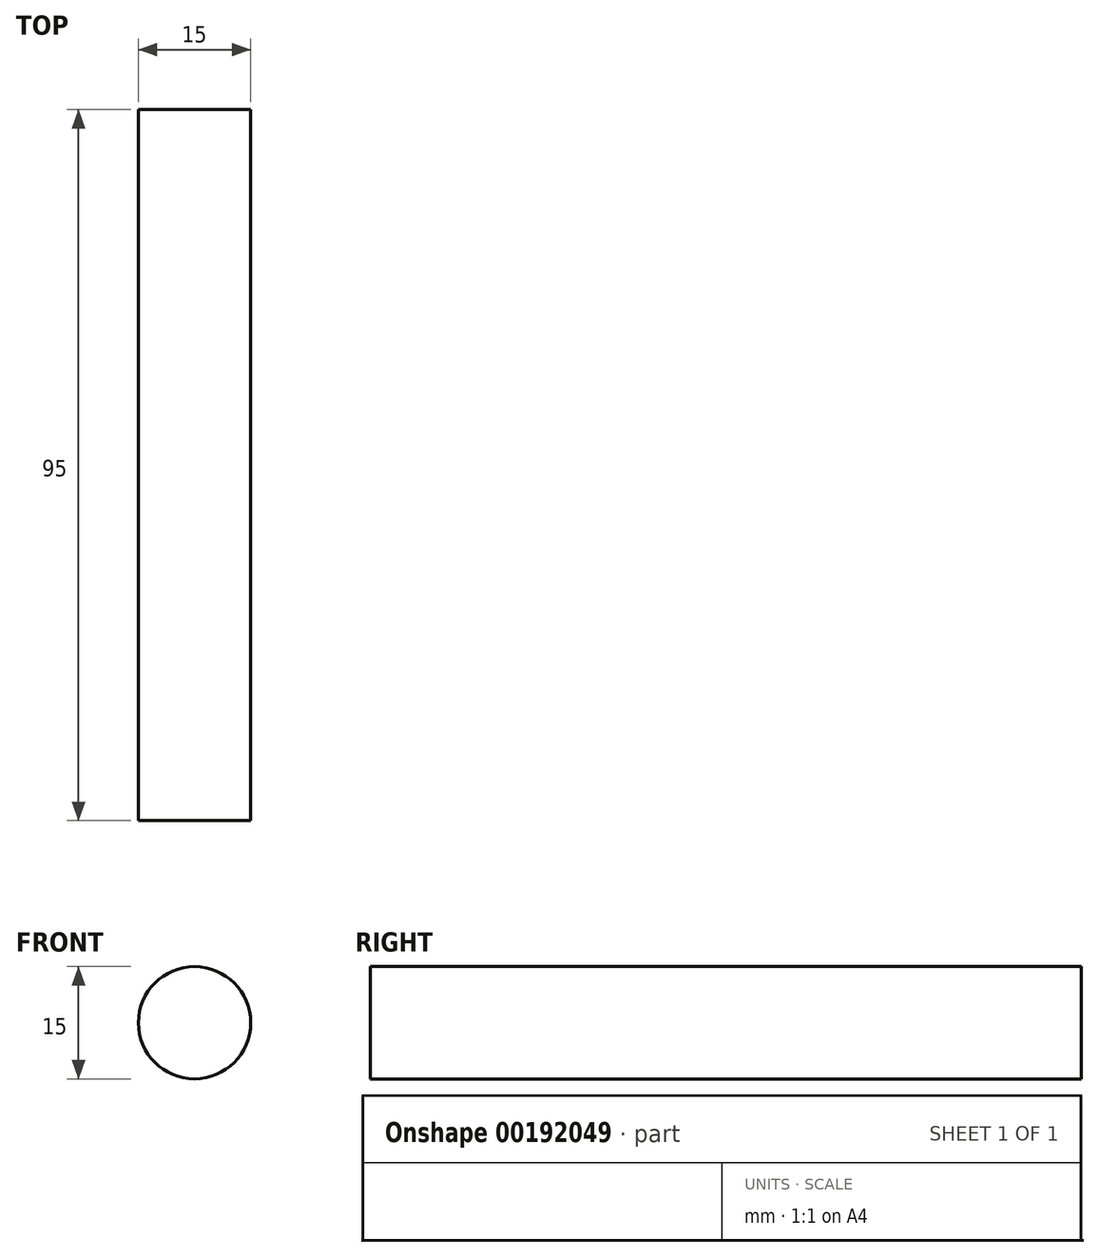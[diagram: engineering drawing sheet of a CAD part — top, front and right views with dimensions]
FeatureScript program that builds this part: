
annotation { "Feature Type Name" : "Feature", "Feature Type Description" : "" }
export const myFeature = defineFeature(function(context is Context, id is Id, definition is map)
    precondition{}
    {
        {
            var Q0;
            Q0=qCreatedBy(makeId("Front.planeOp"),FACE);
            var sketch = newSketch(context, id + "F0", { "sketchPlane" : qUnion([Q0])});
            skCircle(sketch, "E0", {"center": v(-85, 0) * mm, "radius": 4 * mm, "construction": true});
            skCircle(sketch, "E1", {"center": v(85, 0) * mm, "radius": 4 * mm, "construction": true});
            skCircle(sketch, "E2", {"center": v(-85, 0) * mm, "radius": 7.5 * mm});
            skCircle(sketch, "E3", {"center": v(85, 0) * mm, "radius": 7.5 * mm});
            skSolve(sketch);
        }
        {
            var Q0;
            Q0=qCreatedBy(makeId("Top.planeOp"),FACE);
            var sketch = newSketch(context, id + "F1", { "sketchPlane" : qUnion([Q0])});
            skPoint(sketch, "E4.0", {"position": v(-85, 0) * mm});
            skPoint(sketch, "E5.0", {"position": v(85, 0) * mm});
            skLineSegment(sketch, "E6", {"start": v(-85, 47.5) * mm, "end": v(-85, -47.5) * mm});
            skLineSegment(sketch, "E7", {"start": v(85, 12.5) * mm, "end": v(85, -12.5) * mm});
            skLineSegment(sketch, "E8", {"start": v(0, 20.5) * mm, "end": v(0, -20.5) * mm});
            skSolve(sketch);
        }
        {
            var Q0;
            Q0=makeQuery(id+"F0.imprint","IMPRINT",FACE,{"disambiguationData":[TD([[makeQuery(id+"F0.imprint","IMPRINT",EDGE,{"derivedFrom":sQuery(id+"F0.wireOp",EDGE,"E2")}),1.0]])]});
            var Q1;
            Q1=sQuery(id+"F1.wireOp",EDGE,"E6");
            sweep(context, id + "F2", {"profiles" : qUnion([Q0]), "path" : qUnion([Q1])});
        }
    });
